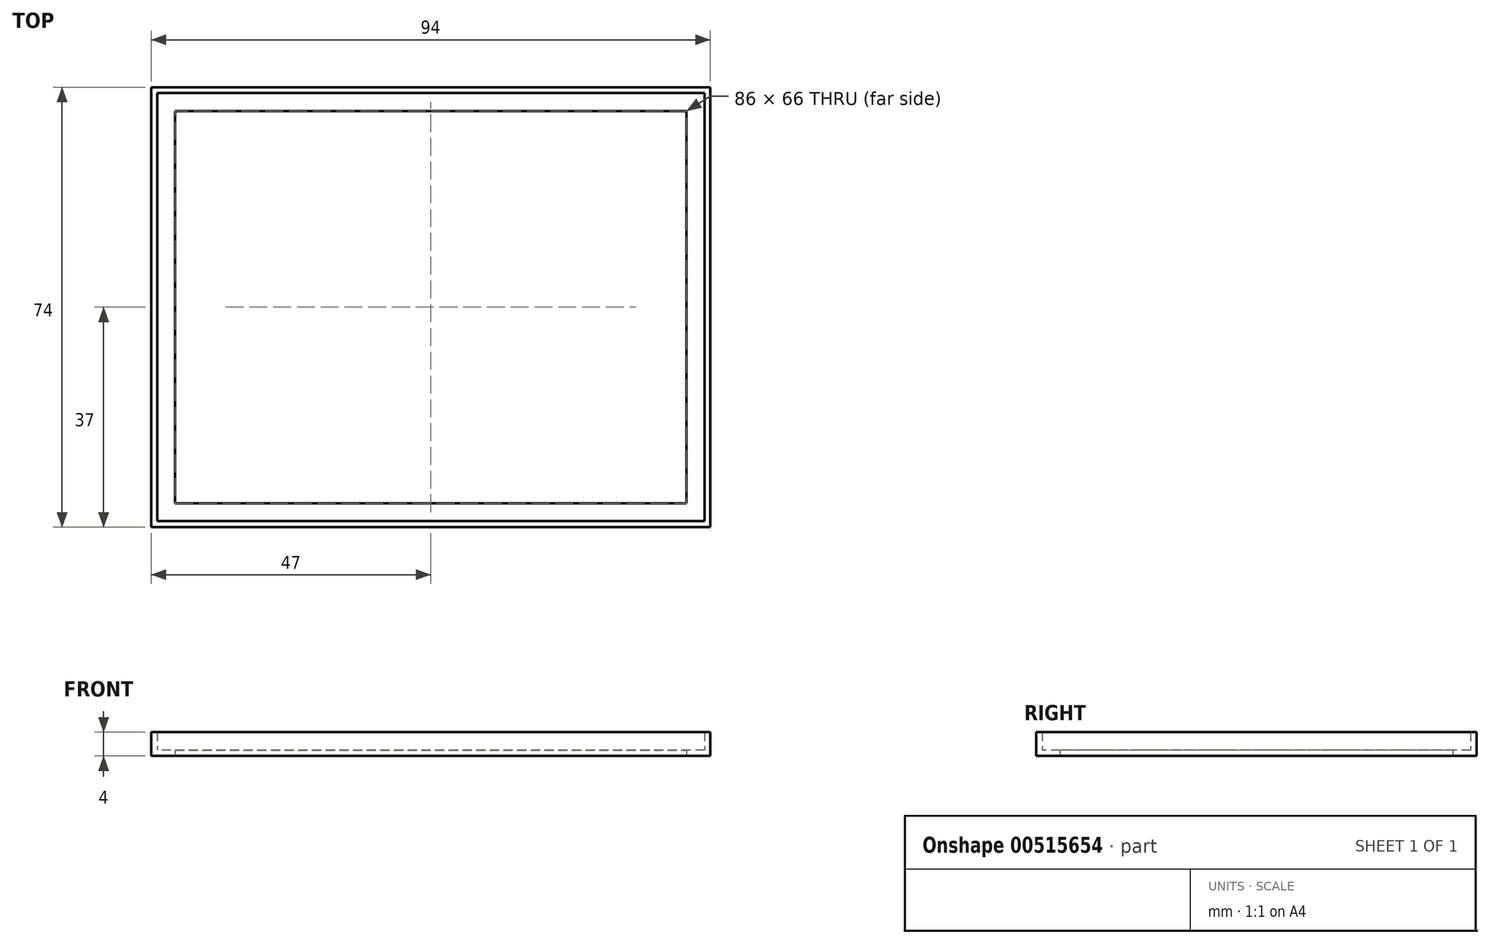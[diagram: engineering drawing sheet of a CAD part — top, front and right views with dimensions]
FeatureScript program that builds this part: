
annotation { "Feature Type Name" : "Feature", "Feature Type Description" : "" }
export const myFeature = defineFeature(function(context is Context, id is Id, definition is map)
    precondition{}
    {
        {
            var Q0;
            Q0=qCreatedBy(makeId("Top.planeOp"),FACE);
            var sketch = newSketch(context, id + "F0", { "sketchPlane" : qUnion([Q0])});
            skLineSegment(sketch, "E0.bottom", {"start": v(46, 36) * mm, "end": v(-46, 36) * mm});
            skLineSegment(sketch, "E0.top", {"start": v(46, -36) * mm, "end": v(-46, -36) * mm});
            skLineSegment(sketch, "E0.left", {"start": v(46, 36) * mm, "end": v(46, -36) * mm});
            skLineSegment(sketch, "E0.right", {"start": v(-46, 36) * mm, "end": v(-46, -36) * mm});
            skPoint(sketch, "E0.middle", {"position": v(0, 0) * mm});
            skLineSegment(sketch, "E1.bottom", {"start": v(47, 37) * mm, "end": v(-47, 37) * mm});
            skLineSegment(sketch, "E1.top", {"start": v(47, -37) * mm, "end": v(-47, -37) * mm});
            skLineSegment(sketch, "E1.left", {"start": v(47, 37) * mm, "end": v(47, -37) * mm});
            skLineSegment(sketch, "E1.right", {"start": v(-47, 37) * mm, "end": v(-47, -37) * mm});
            skPoint(sketch, "E2.endSnap0", {"position": v(0, 37) * mm});
            skLineSegment(sketch, "E3.bottom", {"start": v(-43, 33) * mm, "end": v(43, 33) * mm});
            skLineSegment(sketch, "E3.top", {"start": v(-43, -33) * mm, "end": v(43, -33) * mm});
            skLineSegment(sketch, "E3.left", {"start": v(-43, 33) * mm, "end": v(-43, -33) * mm});
            skLineSegment(sketch, "E3.right", {"start": v(43, 33) * mm, "end": v(43, -33) * mm});
            skSolve(sketch);
        }
        {
            var Q0;
            Q0=makeQuery(id+"F0.imprint","IMPRINT",FACE,{"disambiguationData":[TD([[makeQuery(id+"F0.imprint","IMPRINT",EDGE,{"derivedFrom":sQuery(id+"F0.wireOp",EDGE,"E0.bottom")}),-1.0]])]});
            extrude(context, id + "F1", {"entities" : qUnion([Q0]), "depth" : 4 * mm, "offsetDistance" : 25 * mm});
        }
        {
            var Q0;
            Q0=makeQuery(id+"F0.imprint","IMPRINT",FACE,{"disambiguationData":[TD([[makeQuery(id+"F0.imprint","IMPRINT",EDGE,{"derivedFrom":sQuery(id+"F0.wireOp",EDGE,"E0.bottom")}),1.0]])]});
            extrude(context, id + "F2", {"entities" : qUnion([Q0]), "operationType" : NewBodyOperationType.ADD, "depth" : 1 * mm, "offsetDistance" : 25 * mm});
        }
    });
